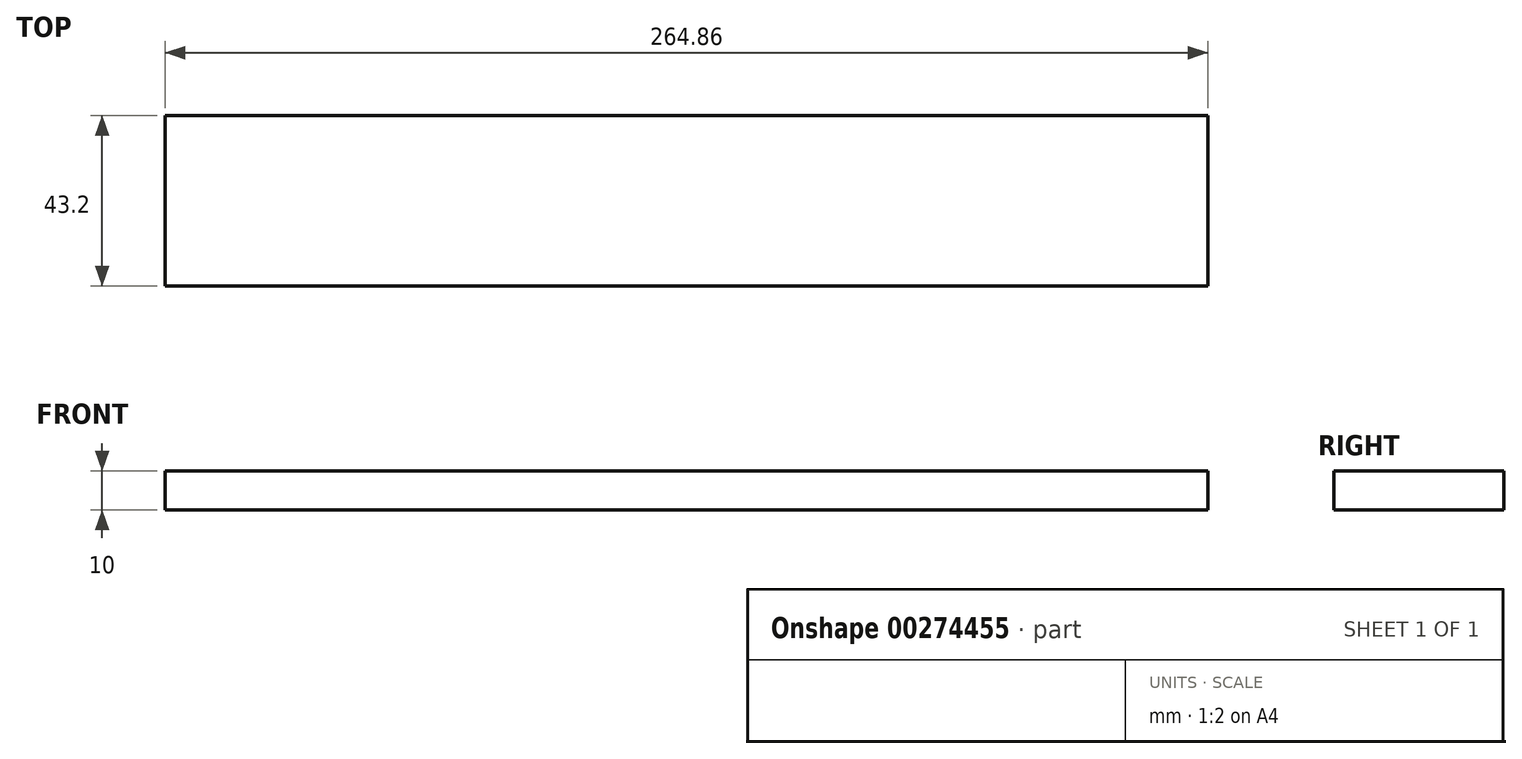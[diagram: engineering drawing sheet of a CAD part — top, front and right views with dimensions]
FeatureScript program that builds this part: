
annotation { "Feature Type Name" : "Feature", "Feature Type Description" : "" }
export const myFeature = defineFeature(function(context is Context, id is Id, definition is map)
    precondition{}
    {
        {
            var Q0;
            Q0=qCreatedBy(makeId("Top.planeOp"),FACE);
            var sketch = newSketch(context, id + "F0", { "sketchPlane" : qUnion([Q0])});
            skLineSegment(sketch, "E0.bottom", {"start": v(-167.27, 17.5) * mm, "end": v(97.6, 17.5) * mm});
            skLineSegment(sketch, "E0.top", {"start": v(-167.27, -25.7) * mm, "end": v(97.6, -25.7) * mm});
            skLineSegment(sketch, "E0.left", {"start": v(-167.27, 17.5) * mm, "end": v(-167.27, -25.7) * mm});
            skLineSegment(sketch, "E0.right", {"start": v(97.6, 17.5) * mm, "end": v(97.6, -25.7) * mm});
            skSolve(sketch);
        }
        {
            var Q0;
            Q0=makeQuery(id+"F0.imprint","IMPRINT",FACE,{"disambiguationData":[TD([[makeQuery(id+"F0.imprint","IMPRINT",EDGE,{"derivedFrom":sQuery(id+"F0.wireOp",EDGE,"E0.bottom")}),-1.0]])]});
            extrude(context, id + "F1", {"entities" : qUnion([Q0]), "depth" : 10 * mm});
        }
    });
